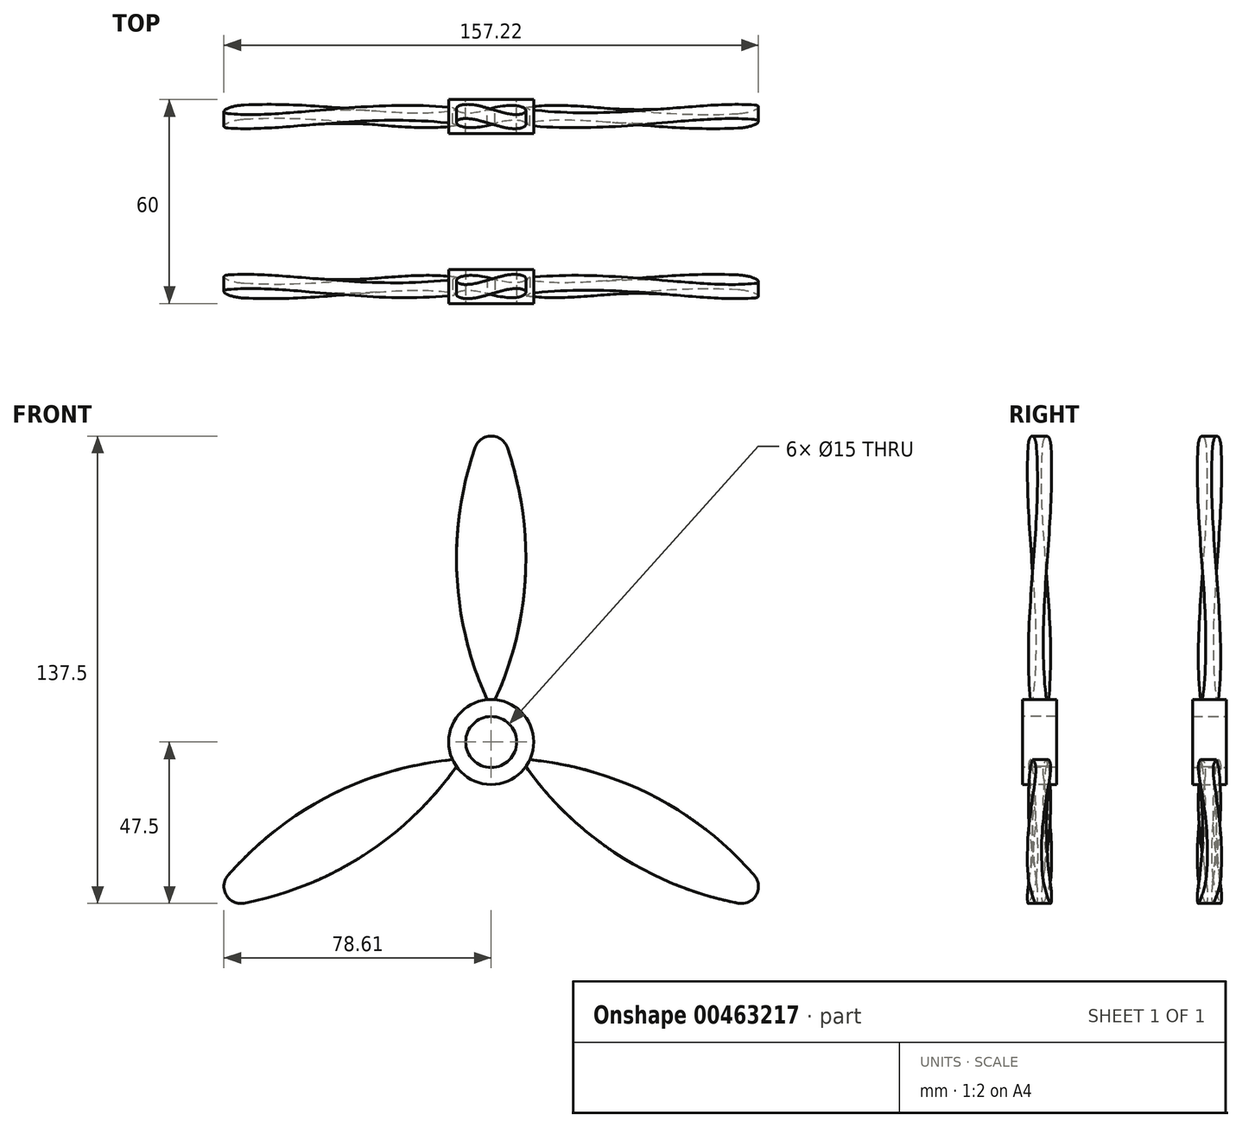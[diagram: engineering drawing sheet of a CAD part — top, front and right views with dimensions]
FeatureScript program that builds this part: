
annotation { "Feature Type Name" : "Feature", "Feature Type Description" : "" }
export const myFeature = defineFeature(function(context is Context, id is Id, definition is map)
    precondition{}
    {
        {
            var Q0;
            Q0=qCreatedBy(makeId("Top.planeOp"),FACE);
            cPlane(context, id + "F0", {"entities" : qUnion([Q0]), "cplaneType" : CPlaneType.OFFSET, "offset" : 100 * mm, "width" : 150 * mm, "height" : 150 * mm});
        }
        {
            var Q0;
            Q0=qCreatedBy(makeId("Top.planeOp"),FACE);
            var sketch = newSketch(context, id + "F1", { "sketchPlane" : qUnion([Q0])});
            skLineSegment(sketch, "E0", {"start": v(0, 31.16) * mm, "end": v(0, -37.4) * mm, "construction": true});
            skLineSegment(sketch, "E1", {"start": v(-32.86, 0) * mm, "end": v(35.13, 0) * mm, "construction": true});
            skLineSegment(sketch, "E2", {"start": v(23.29, 11.04) * mm, "end": v(-23.7, -6.06) * mm});
            skLineSegment(sketch, "E3", {"start": v(-23.7, -6.06) * mm, "end": v(-23.29, -11.04) * mm});
            skLineSegment(sketch, "E4", {"start": v(-23.29, -11.04) * mm, "end": v(23.7, 6.06) * mm});
            skLineSegment(sketch, "E5", {"start": v(23.7, 6.06) * mm, "end": v(23.29, 11.04) * mm});
            skLineSegment(sketch, "E6", {"start": v(23.5, 8.55) * mm, "end": v(-23.5, -8.55) * mm, "construction": true});
            skLineSegment(sketch, "E7", {"start": v(-0.2, 2.5) * mm, "end": v(0.2, -2.5) * mm, "construction": true});
            skSolve(sketch);
        }
        {
            var Q0;
            Q0=qCreatedBy(id+"F0.planeOp",FACE);
            var sketch = newSketch(context, id + "F2", { "sketchPlane" : qUnion([Q0])});
            skLineSegment(sketch, "E8", {"start": v(-33, 0) * mm, "end": v(34.7, 0) * mm, "construction": true});
            skLineSegment(sketch, "E9", {"start": v(0, 31.3) * mm, "end": v(0, -34.98) * mm, "construction": true});
            skLineSegment(sketch, "E10", {"start": v(25.43, -6.98) * mm, "end": v(21.55, -10.12) * mm});
            skLineSegment(sketch, "E11", {"start": v(21.55, -10.12) * mm, "end": v(-25.43, 6.98) * mm});
            skLineSegment(sketch, "E12", {"start": v(-25.43, 6.98) * mm, "end": v(-21.55, 10.12) * mm});
            skLineSegment(sketch, "E13", {"start": v(-23.5, 8.55) * mm, "end": v(23.5, -8.55) * mm, "construction": true});
            skPoint(sketch, "E14.startSnap1", {"position": v(0.85, 0) * mm});
            skLineSegment(sketch, "E15", {"start": v(-21.55, 10.12) * mm, "end": v(25.43, -6.98) * mm});
            skLineSegment(sketch, "E16", {"start": v(-1.94, -1.57) * mm, "end": v(1.94, 1.57) * mm, "construction": true});
            skSolve(sketch);
        }
        {
            var Q0;
            Q0 = qSketchRegion(id + "F1", true);
            var Q1;
            Q1 = qSketchRegion(id + "F2", true);
            loft(context, id + "F3", {"sheetProfilesArray" : [{ "sheetProfileEntities" : qUnion([Q0]) }, { "sheetProfileEntities" : qUnion([Q1]) }]});
        }
        {
            var Q0;
            Q0=qCreatedBy(makeId("Front.planeOp"),FACE);
            var sketch = newSketch(context, id + "F4", { "sketchPlane" : qUnion([Q0])});
            skLineSegment(sketch, "E17", {"start": v(0, 0) * mm, "end": v(0, 101.87) * mm, "construction": true});
            skSolve(sketch);
        }
        {
            var Q0;
            Q0=qCreatedBy(makeId("Front.planeOp"),FACE);
            var sketch = newSketch(context, id + "F5", { "sketchPlane" : qUnion([Q0])});
            skArc(sketch, "E18", {"start": v(0, 10) * mm, "mid": v(10.01, 47.84) * mm, "end": v(4.73, 86.63) * mm});
            skArc(sketch, "E19", {"start": v(4.73, 86.63) * mm, "mid": v(2.9, 89.07) * mm, "end": v(0, 90) * mm});
            skArc(sketch, "E20.MirrorCS", {"start": v(0, 10) * mm, "mid": v(-10.01, 47.84) * mm, "end": v(-4.73, 86.63) * mm});
            skArc(sketch, "E21.MirrorCS", {"start": v(-4.73, 86.63) * mm, "mid": v(-2.9, 89.07) * mm, "end": v(0, 90) * mm});
            skSolve(sketch);
        }
        {
            var Q0;
            Q0 = qSketchRegion(id + "F5", true);
            extrude(context, id + "F6", {"entities" : qUnion([Q0]), "operationType" : NewBodyOperationType.INTERSECT, "endBound" : BoundingType.SYMMETRIC, "depth" : 20 * mm});
        }
        {
            var Q0;
            Q0=qCreatedBy(makeId("Front.planeOp"),FACE);
            var sketch = newSketch(context, id + "F7", { "sketchPlane" : qUnion([Q0])});
            skCircle(sketch, "E22", {"center": v(0, 0) * mm, "radius": 7.5 * mm});
            skCircle(sketch, "E23", {"center": v(0, 0) * mm, "radius": 12.5 * mm});
            skSolve(sketch);
        }
        {
            var Q0;
            Q0=makeQuery(id+"F7.imprint","IMPRINT",FACE,{"disambiguationData":[TD([[makeQuery(id+"F7.imprint","IMPRINT",EDGE,{"derivedFrom":sQuery(id+"F7.wireOp",EDGE,"E22")}),-1.0]])]});
            extrude(context, id + "F8", {"entities" : qUnion([Q0]), "operationType" : NewBodyOperationType.ADD, "endBound" : BoundingType.SYMMETRIC, "depth" : 10 * mm});
        }
        {
            var Q0;
            Q0=makeQuery(id+"F3.opLoft","SWEPT_BODY",BODY,{"disambiguationData":[OSD([makeQuery(id+"F1.imprint","IMPRINT",FACE,{"disambiguationData":[TD([[makeQuery(id+"F1.imprint","IMPRINT",EDGE,{"derivedFrom":sQuery(id+"F1.wireOp",EDGE,"E2")}),1.0]])]}),makeQuery(id+"F2.imprint","IMPRINT",FACE,{"disambiguationData":[TD([[makeQuery(id+"F2.imprint","IMPRINT",EDGE,{"derivedFrom":sQuery(id+"F2.wireOp",EDGE,"E10")}),-1.0]])]})])]});
            var Q1;
            Q1=makeQuery(id+"F8.opExtrude","CAP_EDGE",EDGE,{"disambiguationData":[OSD([sQuery(id+"F7.wireOp",EDGE,"E22")])],"isStart":false});
            circularPattern(context, id + "F9", {"entities" : qUnion([Q0]), "axis" : qUnion([Q1]), "angle" : 360 * degree, "instanceCount" : 3, "equalSpace" : true});
        }
        {
            var Q0;
            Q0=qCreatedBy(makeId("Front.planeOp"),FACE);
            cPlane(context, id + "F10", {"entities" : qUnion([Q0]), "cplaneType" : CPlaneType.OFFSET, "offset" : 25 * mm, "width" : 150 * mm, "height" : 150 * mm});
        }
        {
            var Q0;
            Q0=makeQuery(id+"F3.opLoft","SWEPT_BODY",BODY,{"disambiguationData":[OSD([makeQuery(id+"F1.imprint","IMPRINT",FACE,{"disambiguationData":[TD([[makeQuery(id+"F1.imprint","IMPRINT",EDGE,{"derivedFrom":sQuery(id+"F1.wireOp",EDGE,"E2")}),1.0]])]}),makeQuery(id+"F2.imprint","IMPRINT",FACE,{"disambiguationData":[TD([[makeQuery(id+"F2.imprint","IMPRINT",EDGE,{"derivedFrom":sQuery(id+"F2.wireOp",EDGE,"E10")}),-1.0]])]})])]});
            var Q1;
            Q1=makeQuery(id+"F9.opPattern","COPY",BODY,{"derivedFrom":makeQuery(id+"F3.opLoft","SWEPT_BODY",BODY,{"disambiguationData":[OSD([makeQuery(id+"F1.imprint","IMPRINT",FACE,{"disambiguationData":[TD([[makeQuery(id+"F1.imprint","IMPRINT",EDGE,{"derivedFrom":sQuery(id+"F1.wireOp",EDGE,"E2")}),1.0]])]}),makeQuery(id+"F2.imprint","IMPRINT",FACE,{"disambiguationData":[TD([[makeQuery(id+"F2.imprint","IMPRINT",EDGE,{"derivedFrom":sQuery(id+"F2.wireOp",EDGE,"E10")}),-1.0]])]})])]}),"instanceName":"1"});
            var Q2;
            Q2=makeQuery(id+"F9.opPattern","COPY",BODY,{"derivedFrom":makeQuery(id+"F3.opLoft","SWEPT_BODY",BODY,{"disambiguationData":[OSD([makeQuery(id+"F1.imprint","IMPRINT",FACE,{"disambiguationData":[TD([[makeQuery(id+"F1.imprint","IMPRINT",EDGE,{"derivedFrom":sQuery(id+"F1.wireOp",EDGE,"E2")}),1.0]])]}),makeQuery(id+"F2.imprint","IMPRINT",FACE,{"disambiguationData":[TD([[makeQuery(id+"F2.imprint","IMPRINT",EDGE,{"derivedFrom":sQuery(id+"F2.wireOp",EDGE,"E10")}),-1.0]])]})])]}),"instanceName":"2"});
            var Q3;
            Q3=qCreatedBy(id+"F10.planeOp",FACE);
            mirror(context, id + "F11", {"entities" : qUnion([Q0, Q1, Q2]), "mirrorPlane" : qUnion([Q3])});
        }
    });
